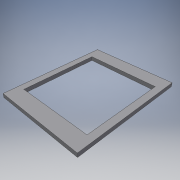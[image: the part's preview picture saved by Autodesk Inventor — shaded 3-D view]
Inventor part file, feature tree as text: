
AUTODESK INVENTOR PART (.ipt)
format: ipt  version: 2016 (Build 200138000, 138)  size: 99,840 bytes
history: native  units: in
note: dims shown in document units (in); Inventor stores cm internally (conversion verified against a paired STEP export)
features: extrude x2, sketch x2
ambient origin geometry x8: Origin, YZ Plane, XZ Plane, XY Plane, X Axis, Y Axis, Z Axis, Center Point
bodies: Solid1 (feature_tree)
feature tree (4):
  extrude  "Extrusion1"  Depth=16.0in
  extrude  "Extrusion2"  Depth=14.5in
  sketch  "Sketch1"  dims[d0=20.0in d1=16.0in]
  sketch  "Sketch2"  dims[d2=0.75in d3=0.0in d4=14.5in d5=13.5in d6=1.0in d7=0.0in]
